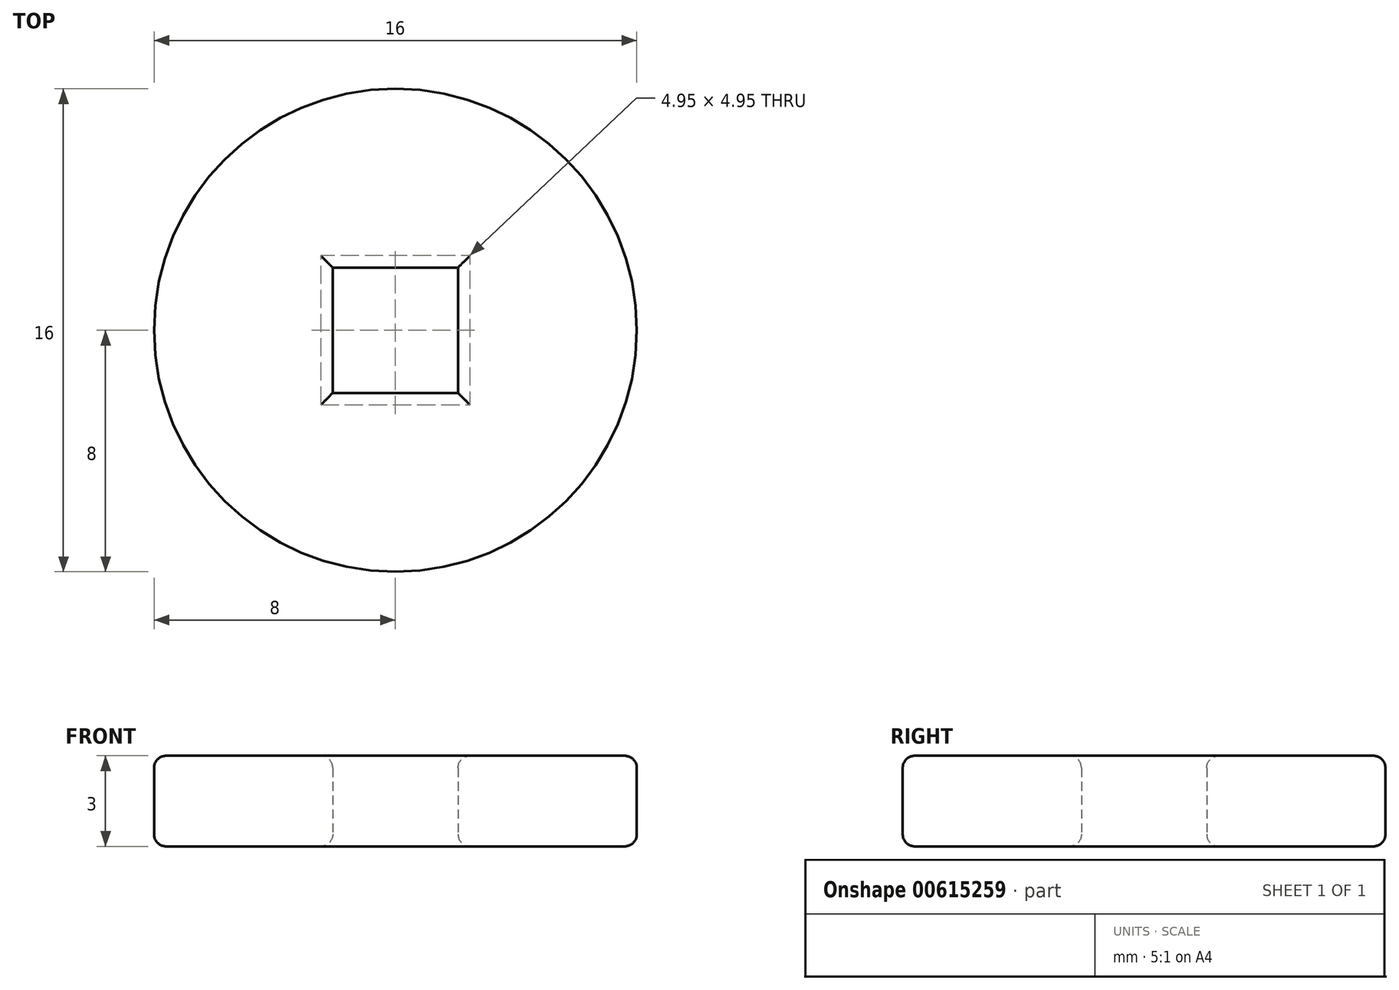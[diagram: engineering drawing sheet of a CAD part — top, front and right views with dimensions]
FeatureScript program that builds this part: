
annotation { "Feature Type Name" : "Feature", "Feature Type Description" : "" }
export const myFeature = defineFeature(function(context is Context, id is Id, definition is map)
    precondition{}
    {
        {
            var Q0;
            Q0=qCreatedBy(makeId("Top.planeOp"),FACE);
            var sketch = newSketch(context, id + "F0", { "sketchPlane" : qUnion([Q0])});
            skCircle(sketch, "E0", {"center": v(0, 0) * mm, "radius": 8 * mm});
            skLineSegment(sketch, "E1.bottom", {"start": v(2.08, -2.08) * mm, "end": v(-2.08, -2.08) * mm});
            skLineSegment(sketch, "E1.top", {"start": v(2.08, 2.08) * mm, "end": v(-2.08, 2.08) * mm});
            skLineSegment(sketch, "E1.left", {"start": v(2.08, -2.08) * mm, "end": v(2.08, 2.08) * mm});
            skLineSegment(sketch, "E1.right", {"start": v(-2.08, -2.08) * mm, "end": v(-2.08, 2.08) * mm});
            skSolve(sketch);
        }
        {
            var Q0;
            Q0=makeQuery(id+"F0.imprint","IMPRINT",FACE,{"disambiguationData":[TD([[makeQuery(id+"F0.imprint","IMPRINT",EDGE,{"derivedFrom":sQuery(id+"F0.wireOp",EDGE,"E0")}),1.0]])]});
            extrude(context, id + "F1", {"entities" : qUnion([Q0]), "depth" : 3 * mm, "offsetDistance" : 25 * mm});
        }
        {
            var Q0;
            Q0=makeQuery(id+"F1.opExtrude","CAP_FACE",FACE,{"disambiguationData":[OSD([sQuery(id+"F0.wireOp",EDGE,"E0"),sQuery(id+"F0.wireOp",EDGE,"E1.bottom"),sQuery(id+"F0.wireOp",EDGE,"E1.top"),sQuery(id+"F0.wireOp",EDGE,"E1.left"),sQuery(id+"F0.wireOp",EDGE,"E1.right")])],"isStart":false});
            var Q1;
            Q1=makeQuery(id+"F1.opExtrude","CAP_FACE",FACE,{"disambiguationData":[OSD([sQuery(id+"F0.wireOp",EDGE,"E0"),sQuery(id+"F0.wireOp",EDGE,"E1.bottom"),sQuery(id+"F0.wireOp",EDGE,"E1.top"),sQuery(id+"F0.wireOp",EDGE,"E1.left"),sQuery(id+"F0.wireOp",EDGE,"E1.right")])],"isStart":true});
            fillet(context, id + "F2", {"entities" : qUnion([Q0, Q1]), "radius" : .4 * mm, "tangentPropagation" : true, "allowEdgeOverflow" : false});
        }
    });
